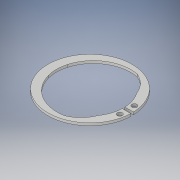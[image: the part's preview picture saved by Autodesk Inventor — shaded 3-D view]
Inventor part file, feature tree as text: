
AUTODESK INVENTOR PART (.ipt)
format: ipt  version: 2018 (Build 220112000, 112)  size: 127,488 bytes
history: native  units: in
note: dims shown in document units (in); Inventor stores cm internally (conversion verified against a paired STEP export)
features: extrude x1, sketch x1
ambient origin geometry x8: Origin, YZ Plane, XZ Plane, XY Plane, X Axis, Y Axis, Z Axis, Center Point
bodies: Solid1 (feature_tree)
feature tree (2):
  extrude  "Extrusion1"  Depth=0.05in
  sketch  "Sketch1"  dims[d0=1.333in d1=1.671in d2=0.025in d3=0.025in d4=0.1in d5=0.169in d6=1.503in d7=0.05in d8=0.0in]
